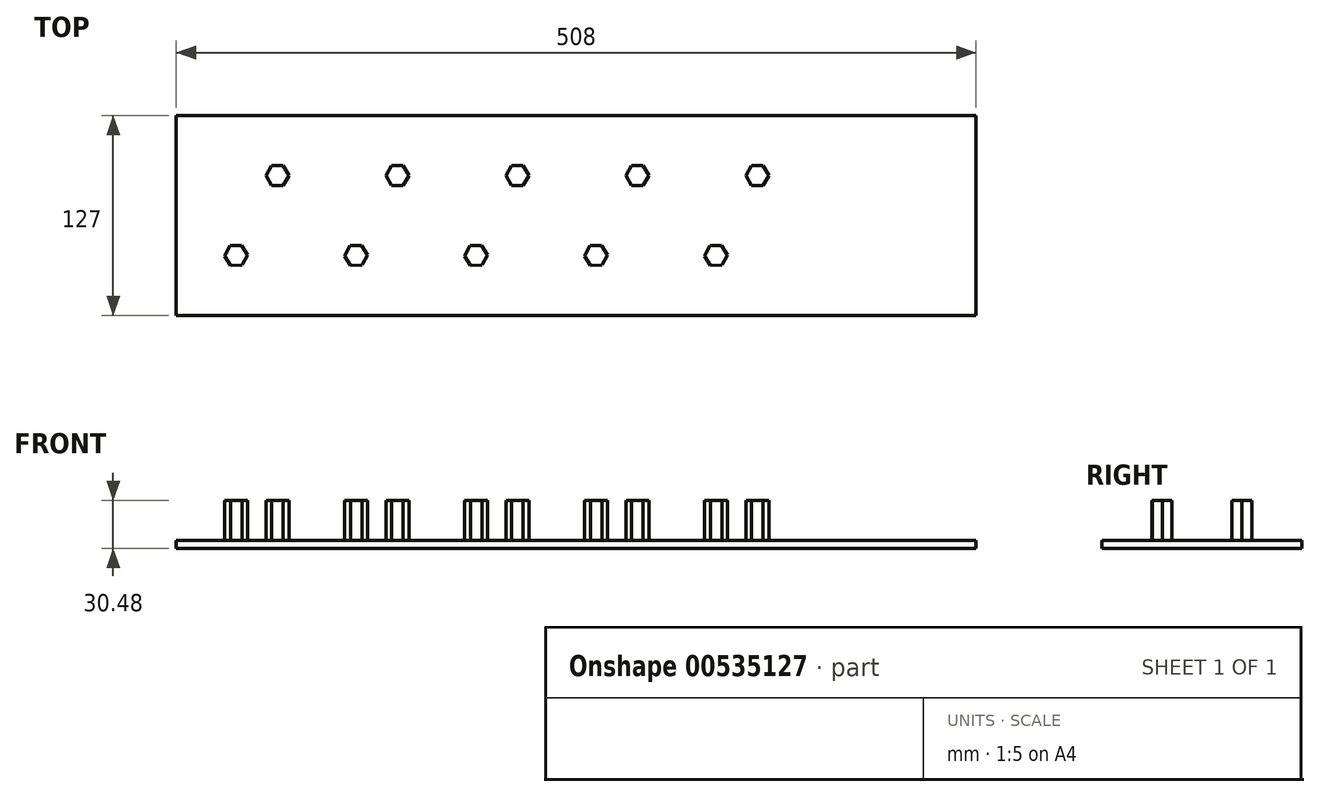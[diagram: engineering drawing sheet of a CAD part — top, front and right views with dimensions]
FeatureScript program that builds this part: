
annotation { "Feature Type Name" : "Feature", "Feature Type Description" : "" }
export const myFeature = defineFeature(function(context is Context, id is Id, definition is map)
    precondition{}
    {
        {
            var Q0;
            Q0=qCreatedBy(makeId("Top.planeOp"),FACE);
            var sketch = newSketch(context, id + "F0", { "sketchPlane" : qUnion([Q0])});
            skLineSegment(sketch, "E0.bottom", {"start": v(0, 0) * mm, "end": v(508, 0) * mm});
            skLineSegment(sketch, "E0.top", {"start": v(0, 127) * mm, "end": v(508, 127) * mm});
            skLineSegment(sketch, "E0.left", {"start": v(0, 0) * mm, "end": v(0, 127) * mm});
            skLineSegment(sketch, "E0.right", {"start": v(508, 0) * mm, "end": v(508, 127) * mm});
            skSolve(sketch);
        }
        {
            var Q0;
            Q0=makeQuery(id+"F0.imprint","IMPRINT",FACE,{"disambiguationData":[TD([[makeQuery(id+"F0.imprint","IMPRINT",EDGE,{"derivedFrom":sQuery(id+"F0.wireOp",EDGE,"E0.bottom")}),1.0]])]});
            extrude(context, id + "F1", {"entities" : qUnion([Q0]), "depth" : 5.08 * mm});
        }
        {
            var Q0;
            Q0=makeQuery(id+"F1.opExtrude","CAP_FACE",FACE,{"disambiguationData":[OSD([sQuery(id+"F0.wireOp",EDGE,"E0.bottom"),sQuery(id+"F0.wireOp",EDGE,"E0.top"),sQuery(id+"F0.wireOp",EDGE,"E0.left"),sQuery(id+"F0.wireOp",EDGE,"E0.right")])],"isStart":false});
            var sketch = newSketch(context, id + "F2", { "sketchPlane" : qUnion([Q0])});
            skCircle(sketch, "E1.cCircle", {"center": v(38.1, 38.1) * mm, "radius": 6.29 * mm, "construction": true});
            skLineSegment(sketch, "E1.0", {"start": v(41.55, 44.49) * mm, "end": v(45.36, 38.3) * mm});
            skLineSegment(sketch, "E1.1", {"start": v(45.36, 38.3) * mm, "end": v(41.9, 31.92) * mm});
            skLineSegment(sketch, "E1.2", {"start": v(41.9, 31.92) * mm, "end": v(34.65, 31.71) * mm});
            skLineSegment(sketch, "E1.3", {"start": v(34.65, 31.71) * mm, "end": v(30.84, 37.9) * mm});
            skLineSegment(sketch, "E1.4", {"start": v(30.84, 37.9) * mm, "end": v(34.3, 44.28) * mm});
            skLineSegment(sketch, "E1.5", {"start": v(34.3, 44.28) * mm, "end": v(41.55, 44.49) * mm});
            skPoint(sketch, "E1.0.midPoint", {"position": v(43.45, 41.4) * mm});
            skCircle(sketch, "E2.cCircle", {"center": v(64.28, 88.9) * mm, "radius": 6.29 * mm, "construction": true});
            skLineSegment(sketch, "E2.0", {"start": v(71.54, 88.9) * mm, "end": v(67.9, 82.6) * mm});
            skLineSegment(sketch, "E2.1", {"start": v(67.9, 82.6) * mm, "end": v(60.64, 82.62) * mm});
            skLineSegment(sketch, "E2.2", {"start": v(60.64, 82.62) * mm, "end": v(57.02, 88.9) * mm});
            skLineSegment(sketch, "E2.3", {"start": v(57.02, 88.9) * mm, "end": v(60.66, 95.2) * mm});
            skLineSegment(sketch, "E2.4", {"start": v(60.66, 95.2) * mm, "end": v(67.92, 95.18) * mm});
            skLineSegment(sketch, "E2.5", {"start": v(67.92, 95.18) * mm, "end": v(71.54, 88.9) * mm});
            skPoint(sketch, "E2.0.midPoint", {"position": v(69.72, 85.75) * mm});
            skLineSegment(sketch, "E3.1.0.0", {"start": v(136.86, 95.2) * mm, "end": v(144.12, 95.18) * mm});
            skLineSegment(sketch, "E3.1.0.1", {"start": v(133.22, 88.9) * mm, "end": v(136.86, 95.2) * mm});
            skLineSegment(sketch, "E3.1.0.2", {"start": v(136.84, 82.62) * mm, "end": v(133.22, 88.9) * mm});
            skLineSegment(sketch, "E3.1.0.3", {"start": v(144.1, 82.6) * mm, "end": v(136.84, 82.62) * mm});
            skLineSegment(sketch, "E3.1.0.4", {"start": v(147.74, 88.9) * mm, "end": v(144.1, 82.6) * mm});
            skLineSegment(sketch, "E3.1.0.5", {"start": v(144.12, 95.18) * mm, "end": v(147.74, 88.9) * mm});
            skLineSegment(sketch, "E3.1.0.6", {"start": v(118.1, 31.92) * mm, "end": v(110.85, 31.71) * mm});
            skLineSegment(sketch, "E3.1.0.7", {"start": v(121.56, 38.3) * mm, "end": v(118.1, 31.92) * mm});
            skLineSegment(sketch, "E3.1.0.8", {"start": v(117.75, 44.49) * mm, "end": v(121.56, 38.3) * mm});
            skLineSegment(sketch, "E3.1.0.9", {"start": v(110.5, 44.28) * mm, "end": v(117.75, 44.49) * mm});
            skLineSegment(sketch, "E3.1.0.10", {"start": v(107.04, 37.9) * mm, "end": v(110.5, 44.28) * mm});
            skLineSegment(sketch, "E3.1.0.11", {"start": v(110.85, 31.71) * mm, "end": v(107.04, 37.9) * mm});
            skLineSegment(sketch, "E3.2.0.0", {"start": v(213.06, 95.2) * mm, "end": v(220.32, 95.18) * mm});
            skLineSegment(sketch, "E3.2.0.1", {"start": v(209.42, 88.9) * mm, "end": v(213.06, 95.2) * mm});
            skLineSegment(sketch, "E3.2.0.2", {"start": v(213.04, 82.62) * mm, "end": v(209.42, 88.9) * mm});
            skLineSegment(sketch, "E3.2.0.3", {"start": v(220.3, 82.6) * mm, "end": v(213.04, 82.62) * mm});
            skLineSegment(sketch, "E3.2.0.4", {"start": v(223.94, 88.9) * mm, "end": v(220.3, 82.6) * mm});
            skLineSegment(sketch, "E3.2.0.5", {"start": v(220.32, 95.18) * mm, "end": v(223.94, 88.9) * mm});
            skLineSegment(sketch, "E3.2.0.6", {"start": v(194.3, 31.92) * mm, "end": v(187.05, 31.71) * mm});
            skLineSegment(sketch, "E3.2.0.7", {"start": v(197.76, 38.3) * mm, "end": v(194.3, 31.92) * mm});
            skLineSegment(sketch, "E3.2.0.8", {"start": v(193.95, 44.49) * mm, "end": v(197.76, 38.3) * mm});
            skLineSegment(sketch, "E3.2.0.9", {"start": v(186.7, 44.28) * mm, "end": v(193.95, 44.49) * mm});
            skLineSegment(sketch, "E3.2.0.10", {"start": v(183.24, 37.9) * mm, "end": v(186.7, 44.28) * mm});
            skLineSegment(sketch, "E3.2.0.11", {"start": v(187.05, 31.71) * mm, "end": v(183.24, 37.9) * mm});
            skLineSegment(sketch, "E3.3.0.0", {"start": v(289.26, 95.2) * mm, "end": v(296.52, 95.18) * mm});
            skLineSegment(sketch, "E3.3.0.1", {"start": v(285.62, 88.9) * mm, "end": v(289.26, 95.2) * mm});
            skLineSegment(sketch, "E3.3.0.2", {"start": v(289.24, 82.62) * mm, "end": v(285.62, 88.9) * mm});
            skLineSegment(sketch, "E3.3.0.3", {"start": v(296.5, 82.6) * mm, "end": v(289.24, 82.62) * mm});
            skLineSegment(sketch, "E3.3.0.4", {"start": v(300.14, 88.9) * mm, "end": v(296.5, 82.6) * mm});
            skLineSegment(sketch, "E3.3.0.5", {"start": v(296.52, 95.18) * mm, "end": v(300.14, 88.9) * mm});
            skLineSegment(sketch, "E3.3.0.6", {"start": v(270.5, 31.92) * mm, "end": v(263.25, 31.71) * mm});
            skLineSegment(sketch, "E3.3.0.7", {"start": v(273.96, 38.3) * mm, "end": v(270.5, 31.92) * mm});
            skLineSegment(sketch, "E3.3.0.8", {"start": v(270.15, 44.49) * mm, "end": v(273.96, 38.3) * mm});
            skLineSegment(sketch, "E3.3.0.9", {"start": v(262.9, 44.28) * mm, "end": v(270.15, 44.49) * mm});
            skLineSegment(sketch, "E3.3.0.10", {"start": v(259.44, 37.9) * mm, "end": v(262.9, 44.28) * mm});
            skLineSegment(sketch, "E3.3.0.11", {"start": v(263.25, 31.71) * mm, "end": v(259.44, 37.9) * mm});
            skLineSegment(sketch, "E3.4.0.0", {"start": v(365.46, 95.2) * mm, "end": v(372.72, 95.18) * mm});
            skLineSegment(sketch, "E3.4.0.1", {"start": v(361.82, 88.9) * mm, "end": v(365.46, 95.2) * mm});
            skLineSegment(sketch, "E3.4.0.2", {"start": v(365.44, 82.62) * mm, "end": v(361.82, 88.9) * mm});
            skLineSegment(sketch, "E3.4.0.3", {"start": v(372.7, 82.6) * mm, "end": v(365.44, 82.62) * mm});
            skLineSegment(sketch, "E3.4.0.4", {"start": v(376.34, 88.9) * mm, "end": v(372.7, 82.6) * mm});
            skLineSegment(sketch, "E3.4.0.5", {"start": v(372.72, 95.18) * mm, "end": v(376.34, 88.9) * mm});
            skLineSegment(sketch, "E3.4.0.6", {"start": v(346.7, 31.92) * mm, "end": v(339.45, 31.71) * mm});
            skLineSegment(sketch, "E3.4.0.7", {"start": v(350.16, 38.3) * mm, "end": v(346.7, 31.92) * mm});
            skLineSegment(sketch, "E3.4.0.8", {"start": v(346.35, 44.49) * mm, "end": v(350.16, 38.3) * mm});
            skLineSegment(sketch, "E3.4.0.9", {"start": v(339.1, 44.28) * mm, "end": v(346.35, 44.49) * mm});
            skLineSegment(sketch, "E3.4.0.10", {"start": v(335.64, 37.9) * mm, "end": v(339.1, 44.28) * mm});
            skLineSegment(sketch, "E3.4.0.11", {"start": v(339.45, 31.71) * mm, "end": v(335.64, 37.9) * mm});
            skLineSegment(sketch, "E3.direction1", {"start": v(60.66, 95.2) * mm, "end": v(136.86, 95.2) * mm, "construction": true});
            skSolve(sketch);
        }
        {
            var Q0;
            Q0=qSketchRegion(id+"F2",true);
            extrude(context, id + "F3", {"entities" : qUnion([Q0]), "operationType" : NewBodyOperationType.ADD, "depth" : 25.4 * mm});
        }
    });
